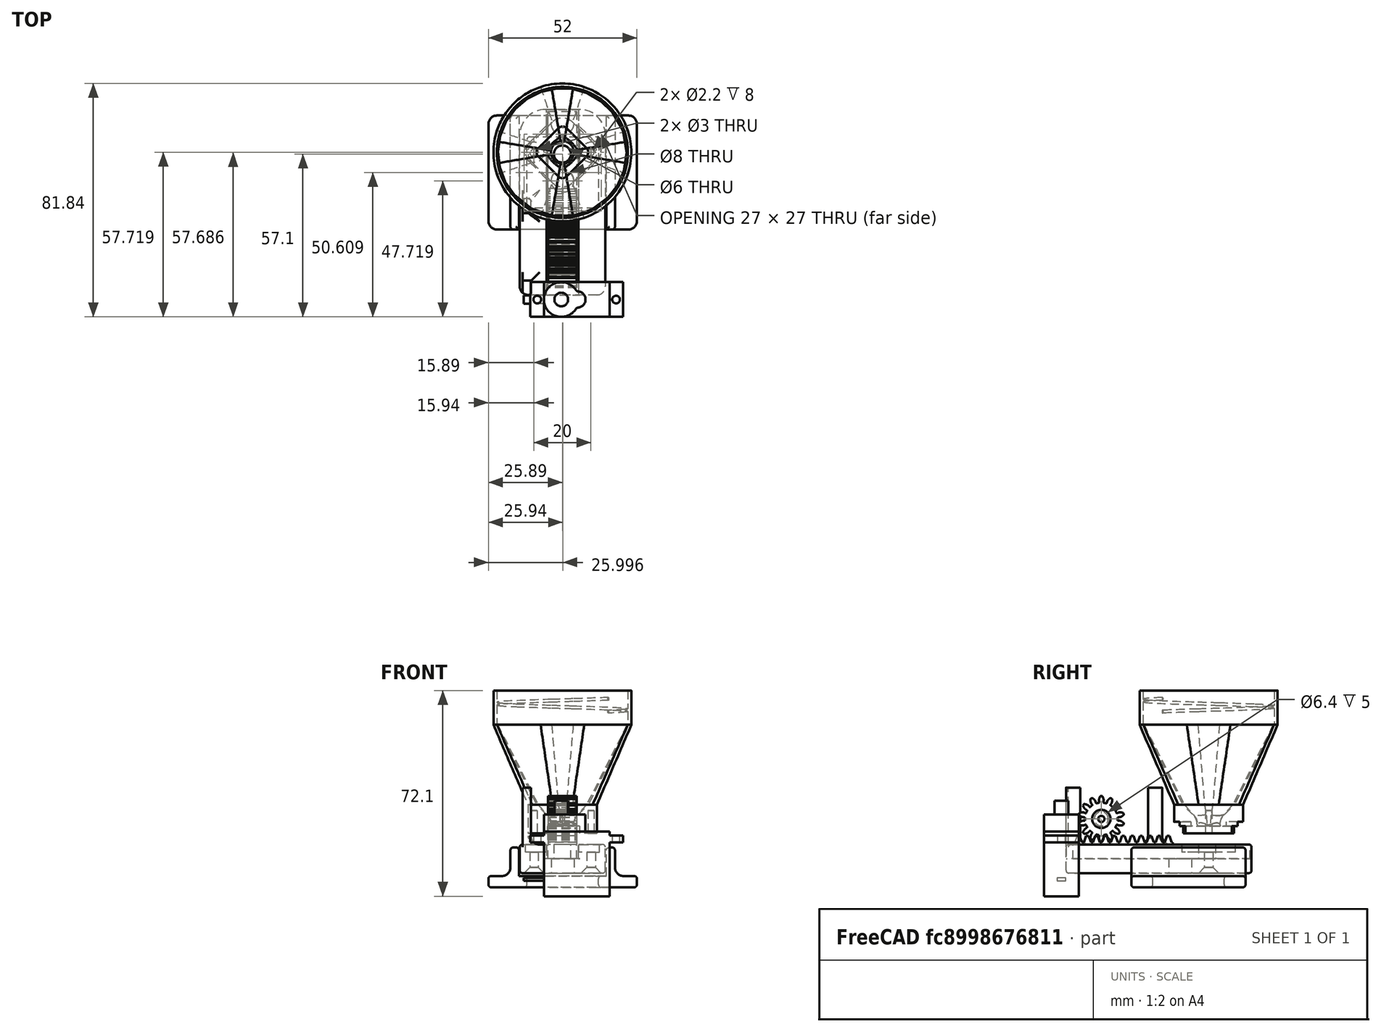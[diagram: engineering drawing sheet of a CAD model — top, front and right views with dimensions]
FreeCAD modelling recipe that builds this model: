
FCSTD DOCUMENT  (FreeCAD 0.19R24267 +148 (Git))
Label: aqua-feeder-v2
License: All rights reserved
LicenseURL: http://en.wikipedia.org/wiki/All_rights_reserved
objects: Sketcher::SketchObject×26, PartDesign::Fillet×15, PartDesign::Pad×11, PartDesign::Pocket×8, PartDesign::Body×6, PartDesign::FeaturePython×2, PartDesign::AdditiveLoft×1, PartDesign::AdditiveHelix×1, Spreadsheet::Sheet×1, App::Part×1, PartDesign::Chamfer×1
note: 108 computed .brp shape members not serialized (recipe doc carries the construction recipe); baked Part::Feature solids carry a one-line shape summary decoded from their .brp

FEATURE [Sketcher::SketchObject] Sketch
  FullyConstrained = true
  MapMode = 5
  Support = -> [XY_Plane]
  expr: Constraints[1] = 45.9 / 2
  expr: Constraints[3] = 45.9 / 2 + 0.6 * 2
  sketch-geometry (2):
    g0: Circle CenterX=0 CenterY=0 CenterZ=0 NormalX=0 NormalY=0 NormalZ=1 AngleXU=0 Radius=22.95
    g1: Circle CenterX=0 CenterY=0 CenterZ=0 NormalX=0 NormalY=0 NormalZ=1 AngleXU=0 Radius=24.15
  constraints (4):
    c: Coincident(g0,g-1)
    c: Radius(g0) = 22.95
    c: Coincident(g1,g0)
    c: Radius(g1) = 24.15
FEATURE [Sketcher::SketchObject] Sketch001
  AttachmentOffset = pos=(0,0,40) rot=(0,0,1;0rad)
  FullyConstrained = true
  MapMode = 5
  Placement = pos=(0,0,40) rot=(0,0,1;0rad)
  Support = -> [XY_Plane]
  sketch-geometry (16):
    g0: LineSegment StartX=-5 StartY=7 StartZ=0 EndX=5 EndY=7 EndZ=0
    g1: LineSegment StartX=7 StartY=5 StartZ=0 EndX=7 EndY=-5 EndZ=0
    g2: LineSegment StartX=5 StartY=-7 StartZ=0 EndX=-5 EndY=-7 EndZ=0
    g3: LineSegment StartX=-7 StartY=-5 StartZ=0 EndX=-7 EndY=5 EndZ=0
    g4: ArcOfCircle CenterX=-5 CenterY=-5 CenterZ=0 NormalX=0 NormalY=0 NormalZ=1 AngleXU=0 Radius=2 StartAngle=3.14159 EndAngle=4.71239
    g5: ArcOfCircle CenterX=5 CenterY=-5 CenterZ=0 NormalX=0 NormalY=0 NormalZ=1 AngleXU=0 Radius=2 StartAngle=4.71239 EndAngle=6.28319
    g6: ArcOfCircle CenterX=5 CenterY=5 CenterZ=0 NormalX=0 NormalY=0 NormalZ=1 AngleXU=0 Radius=2 StartAngle=0 EndAngle=1.5708
    g7: ArcOfCircle CenterX=-5 CenterY=5 CenterZ=0 NormalX=0 NormalY=0 NormalZ=1 AngleXU=0 Radius=2 StartAngle=1.5708 EndAngle=3.14159
    g8: LineSegment StartX=-5 StartY=10 StartZ=0 EndX=5 EndY=10 EndZ=0
    g9: LineSegment StartX=10 StartY=5 StartZ=0 EndX=10 EndY=-5 EndZ=0
    g10: LineSegment StartX=5 StartY=-10 StartZ=0 EndX=-5 EndY=-10 EndZ=0
    g11: LineSegment StartX=-10 StartY=-5 StartZ=0 EndX=-10 EndY=5 EndZ=0
    g12: ArcOfCircle CenterX=5 CenterY=5 CenterZ=0 NormalX=0 NormalY=0 NormalZ=1 AngleXU=0 Radius=5 StartAngle=1.5e-15 EndAngle=1.5708
    g13: ArcOfCircle CenterX=5 CenterY=-5 CenterZ=0 NormalX=0 NormalY=0 NormalZ=1 AngleXU=0 Radius=5 StartAngle=4.71239 EndAngle=6.28319
    g14: ArcOfCircle CenterX=-5 CenterY=-5 CenterZ=0 NormalX=0 NormalY=0 NormalZ=1 AngleXU=0 Radius=5 StartAngle=3.14159 EndAngle=4.71239
    g15: ArcOfCircle CenterX=-5 CenterY=5 CenterZ=0 NormalX=0 NormalY=0 NormalZ=1 AngleXU=0 Radius=5 StartAngle=1.5708 EndAngle=3.14159
  constraints (37):
    c: Horizontal(g0)
    c: Horizontal(g2)
    c: Vertical(g1)
    c: Vertical(g3)
    c: Tangent(g2,g4) = 1.5708
    c: Tangent(g3,g4) = 1.5708
    c: Tangent(g2,g5) = 1.5708
    c: Tangent(g1,g5) = 1.5708
    c: Tangent(g0,g6) = 1.5708
    c: Tangent(g1,g6) = 1.5708
    c: Tangent(g3,g7) = 1.5708
    c: Tangent(g0,g7) = 1.5708
    c: Equal(g6,g5)
    c: Equal(g5,g4)
    c: Equal(g4,g7)
    c: Symmetric(g7,g5,g-1)
    c: Radius(g7) = 2
    c: Horizontal(g8)
    c: Horizontal(g10)
    c: Vertical(g9)
    c: Vertical(g11)
    c: Tangent(g8,g12) = 1.5708
    c: Tangent(g9,g12) = 1.5708
    c: Tangent(g10,g13) = 1.5708
    c: Tangent(g9,g13) = 1.5708
    c: Tangent(g10,g14) = 1.5708
    c: Tangent(g11,g14) = 1.5708
    c: Tangent(g11,g15) = 1.5708
    c: Tangent(g8,g15) = 1.5708
    c: Equal(g15,g12)
    c: Equal(g12,g13)
    c: Equal(g13,g14)
    c: Coincident(g15,g7)
    c: Coincident(g13,g5)
    c: DistanceX(g11,g3) = 3
    c: DistanceX(g11,g9) = 20
    c: DistanceY(g10,g8) = 20
FEATURE [Sketcher::SketchObject] Sketch002  label="thread"
  FullyConstrained = true
  MapMode = 3
  Placement = pos=(0,0,0) rot=(1,0,0;1.5708rad)
  sketch-geometry (2):
    g0: LineSegment StartX=-23 StartY=2.4 StartZ=0 EndX=-23 EndY=3.4 EndZ=0
    g1: ArcOfCircle CenterX=-23 CenterY=2.9 CenterZ=0 NormalX=0 NormalY=0 NormalZ=1 AngleXU=0 Radius=0.5 StartAngle=4.71239 EndAngle=7.85398
  constraints (7):
    c: Vertical(g0)
    c: DistanceY(g-1,g0) = 2.4
    c: Coincident(g1,g0)
    c: Coincident(g1,g0)
    c: PointOnObject(g1,g0)
    c: Radius(g1) = 0.5
    c: DistanceX(g0,g-1) = 23
FEATURE [Sketcher::SketchObject] Sketch004
  AttachmentOffset = pos=(0,0,50) rot=(0,0,1;0rad)
  ExternalGeometry = -> [Sketch001]
  FullyConstrained = false
  MapMode = 5
  Placement = pos=(0,0,50) rot=(0,0,1;0rad)
  Support = -> [XY_Plane]
  sketch-geometry (9):
    g0: Circle CenterX=0 CenterY=0 CenterZ=0 NormalX=0 NormalY=0 NormalZ=1 AngleXU=0 Radius=4
    g1: LineSegment StartX=-5 StartY=10 StartZ=0 EndX=5 EndY=10 EndZ=0
    g2: LineSegment StartX=10 StartY=5 StartZ=0 EndX=10 EndY=-5 EndZ=0
    g3: LineSegment StartX=5 StartY=-10 StartZ=0 EndX=-5 EndY=-10 EndZ=0
    g4: LineSegment StartX=-10 StartY=-5 StartZ=0 EndX=-10 EndY=5 EndZ=0
    g5: ArcOfCircle CenterX=5 CenterY=5 CenterZ=0 NormalX=0 NormalY=0 NormalZ=1 AngleXU=0 Radius=5 StartAngle=-1.8e-15 EndAngle=1.5708
    g6: ArcOfCircle CenterX=5 CenterY=-5 CenterZ=0 NormalX=0 NormalY=0 NormalZ=1 AngleXU=0 Radius=5 StartAngle=4.71239 EndAngle=6.28319
    g7: ArcOfCircle CenterX=-5 CenterY=-5 CenterZ=0 NormalX=0 NormalY=0 NormalZ=1 AngleXU=0 Radius=5 StartAngle=3.14159 EndAngle=4.71239
    g8: ArcOfCircle CenterX=-5 CenterY=5 CenterZ=0 NormalX=0 NormalY=0 NormalZ=1 AngleXU=0 Radius=5 StartAngle=1.5708 EndAngle=3.14159
  constraints (16):
    c: Coincident(g0,g-1)
    c: Radius(g0) = 4
    c: Horizontal(g1)
    c: Horizontal(g3)
    c: Vertical(g4)
    c: Tangent(g1,g5) = 1.5708
    c: Tangent(g2,g5) = 1.5708
    c: Tangent(g3,g6) = 1.5708
    c: Tangent(g2,g6) = 1.5708
    c: Tangent(g3,g7) = 1.5708
    c: Tangent(g4,g7) = 1.5708
    c: Tangent(g4,g8) = 1.5708
    c: Tangent(g1,g8) = 1.5708
    c: Equal(g8,g5)
    c: Equal(g5,g6)
    c: Equal(g6,g7)
FEATURE [Sketcher::SketchObject] Sketch005
  AttachmentOffset = pos=(0,0,12) rot=(0,0,1;0rad)
  FullyConstrained = true
  MapMode = 5
  Placement = pos=(0,0,12) rot=(0,0,1;0rad)
  Support = -> [XY_Plane]
  expr: Constraints[1] = 45.9 / 2
  expr: Constraints[3] = 45.9 / 2 + 0.6 * 2
  sketch-geometry (2):
    g0: Circle CenterX=0 CenterY=0 CenterZ=0 NormalX=0 NormalY=0 NormalZ=1 AngleXU=0 Radius=22.95
    g1: Circle CenterX=0 CenterY=0 CenterZ=0 NormalX=0 NormalY=0 NormalZ=1 AngleXU=0 Radius=24.15
  constraints (4):
    c: Coincident(g0,g-1)
    c: Radius(g0) = 22.95
    c: Coincident(g1,g0)
    c: Radius(g1) = 24.15
FEATURE [Sketcher::SketchObject] Sketch006  label="mount-holes"
  AttachmentOffset = pos=(0,0,50) rot=(0,0,1;0rad)
  FullyConstrained = true
  MapMode = 5
  Placement = pos=(0,0,50) rot=(0,0,1;0rad)
  Support = -> [XY_Plane]
  sketch-geometry (3):
    g0: Circle CenterX=-7.07107 CenterY=7.07107 CenterZ=0 NormalX=0 NormalY=0 NormalZ=1 AngleXU=0 Radius=1.1
    g1: Circle CenterX=7.07107 CenterY=-7.07107 CenterZ=0 NormalX=0 NormalY=0 NormalZ=1 AngleXU=0 Radius=1.1
    g2: LineSegment StartX=7.07107 StartY=-7.07107 StartZ=0 EndX=-7.07107 EndY=7.07107 EndZ=0
  constraints (7):
    c: Symmetric(g1,g0,g-1)
    c: Equal(g0,g1)
    c: Radius(g1) = 1.1
    c: Distance(g1,g0) = 20
    c: Coincident(g2,g1)
    c: Coincident(g2,g0)
    c: Angle(g2,g-1) = 0.785398
FEATURE [Sketcher::SketchObject] Sketch007
  AttachmentOffset = pos=(0,0,45) rot=(0,0,1;0rad)
  ExternalGeometry = -> [Sketch001]
  FullyConstrained = false
  MapMode = 5
  Placement = pos=(0,0,45) rot=(0,0,1;0rad)
  Support = -> [XY_Plane]
  sketch-geometry (9):
    g0: Circle CenterX=0 CenterY=0 CenterZ=0 NormalX=0 NormalY=0 NormalZ=1 AngleXU=0 Radius=4
    g1: LineSegment StartX=-5 StartY=10 StartZ=0 EndX=5 EndY=10 EndZ=0
    g2: LineSegment StartX=10 StartY=5 StartZ=0 EndX=10 EndY=-5 EndZ=0
    g3: LineSegment StartX=5 StartY=-10 StartZ=0 EndX=-5 EndY=-10 EndZ=0
    g4: LineSegment StartX=-10 StartY=-5 StartZ=0 EndX=-10 EndY=5 EndZ=0
    g5: ArcOfCircle CenterX=5 CenterY=5 CenterZ=0 NormalX=0 NormalY=0 NormalZ=1 AngleXU=0 Radius=5 StartAngle=-1.8e-15 EndAngle=1.5708
    g6: ArcOfCircle CenterX=5 CenterY=-5 CenterZ=0 NormalX=0 NormalY=0 NormalZ=1 AngleXU=0 Radius=5 StartAngle=4.71239 EndAngle=6.28319
    g7: ArcOfCircle CenterX=-5 CenterY=-5 CenterZ=0 NormalX=0 NormalY=0 NormalZ=1 AngleXU=0 Radius=5 StartAngle=3.14159 EndAngle=4.71239
    g8: ArcOfCircle CenterX=-5 CenterY=5 CenterZ=0 NormalX=0 NormalY=0 NormalZ=1 AngleXU=0 Radius=5 StartAngle=1.5708 EndAngle=3.14159
  constraints (16):
    c: Coincident(g0,g-1)
    c: Radius(g0) = 4
    c: Horizontal(g1)
    c: Horizontal(g3)
    c: Vertical(g4)
    c: Tangent(g1,g5) = 1.5708
    c: Tangent(g2,g5) = 1.5708
    c: Tangent(g3,g6) = 1.5708
    c: Tangent(g2,g6) = 1.5708
    c: Tangent(g3,g7) = 1.5708
    c: Tangent(g4,g7) = 1.5708
    c: Tangent(g4,g8) = 1.5708
    c: Tangent(g1,g8) = 1.5708
    c: Equal(g8,g5)
    c: Equal(g5,g6)
    c: Equal(g6,g7)
FEATURE [PartDesign::AdditiveLoft] AdditiveLoft  label="body001"
  Closed = false
  Profile = -> Sketch
  Refine = true
  Ruled = true
  Sections = -> [Sketch005,Sketch001,Sketch007,Sketch004]
FEATURE [PartDesign::Pocket] Pocket  label="mount-holes001"
  BaseFeature = -> AdditiveLoft
  Length = 8
  Length2 = 100
  Profile = -> Sketch006
  Type = 0
FEATURE [Sketcher::SketchObject] Sketch008
  AttachmentOffset = pos=(0,0,50) rot=(0,0,1;0rad)
  FullyConstrained = false
  MapMode = 5
  Placement = pos=(0,0,50) rot=(0,0,1;0rad)
  Support = -> [XY_Plane]
  sketch-geometry (5):
    g0: LineSegment StartX=-29.8042 StartY=-29.8042 StartZ=0 EndX=30.9142 EndY=30.9142 EndZ=0
    g1: LineSegment StartX=-25.7953 StartY=-17.3431 StartZ=0 EndX=-17.8757 EndY=-25.2627 EndZ=0
    g2: LineSegment StartX=-17.8757 StartY=-25.2627 StartZ=0 EndX=26.0543 EndY=18.6672 EndZ=0
    g3: LineSegment StartX=26.0543 StartY=18.6672 StartZ=0 EndX=18.1347 EndY=26.5868 EndZ=0
    g4: LineSegment StartX=18.1347 StartY=26.5868 StartZ=0 EndX=-25.7953 EndY=-17.3431 EndZ=0
  constraints (11):
    c: PointOnObject(g-1,g0)
    c: Angle(g-1,g0) = 0.785398
    c: Coincident(g1,g2)
    c: Coincident(g2,g3)
    c: Coincident(g3,g4)
    c: Coincident(g4,g1)
    c: Equal(g1,g3)
    c: Equal(g2,g4)
    c: Perpendicular(g3,g2)
    c: Perpendicular(g0,g3)
    c: Distance(g1) = 11.2
FEATURE [PartDesign::Pocket] Pocket001  label="slider-wedge"
  BaseFeature = -> Pocket
  Length = 2.5
  Length2 = 100
  Profile = -> Sketch008
  Type = 0
FEATURE [PartDesign::AdditiveHelix] AdditiveHelix  label="thread001"
  Angle = 0
  Axis = (-3e-16,3e-16,1)
  Base = (0,0,0)
  BaseFeature = -> Pocket001
  HasBeenEdited = true
  Height = 4.5
  LeftHanded = false
  Mode = 1
  Outside = false
  Pitch = 4.5
  Profile = -> Sketch002
  ReferenceAxis = -> Z_Axis
  Turns = 1
FEATURE [Sketcher::SketchObject] Sketch009
  AttachmentOffset = pos=(0,0,50) rot=(0,0,1;0rad)
  FullyConstrained = false
  MapMode = 5
  Placement = pos=(0,0,50) rot=(0,0,1;0rad)
  Support = -> [XY_Plane]
  sketch-geometry (3):
    g0: Circle CenterX=7.18002 CenterY=7.18002 CenterZ=0 NormalX=0 NormalY=0 NormalZ=1 AngleXU=0 Radius=4
    g1: Circle CenterX=-7.18002 CenterY=-7.18002 CenterZ=0 NormalX=0 NormalY=0 NormalZ=1 AngleXU=0 Radius=4
    g2: LineSegment StartX=-7.18002 StartY=-7.18002 StartZ=0 EndX=7.18002 EndY=7.18002 EndZ=0
  constraints (6):
    c: Symmetric(g1,g0,g-1)
    c: Coincident(g2,g1)
    c: Coincident(g2,g0)
    c: Angle(g2,g-1) = -0.785398
    c: Equal(g1,g0)
    c: Radius(g1) = 4
FEATURE [PartDesign::Pocket] Pocket002  label="air-relief"
  BaseFeature = -> AdditiveHelix
  Length = 4
  Length2 = 100
  Profile = -> Sketch009
  Type = 0
FEATURE [Sketcher::SketchObject] Sketch010
  FullyConstrained = false
  MapMode = 5
  Support = -> [XY_Plane001]
  sketch-geometry (10):
    g0: LineSegment StartX=-45.9619 StartY=-24.7487 StartZ=0 EndX=0 EndY=21.2132 EndZ=0
    g1: LineSegment StartX=0 StartY=21.2132 StartZ=0 EndX=21.2132 EndY=-3.6e-15 EndZ=0
    g2: LineSegment StartX=21.2132 StartY=-3.6e-15 StartZ=0 EndX=-24.7487 EndY=-45.9619 EndZ=0
    g3: LineSegment StartX=-24.7487 StartY=-45.9619 StartZ=0 EndX=-45.9619 EndY=-24.7487 EndZ=0
    g4: LineSegment StartX=-48.6553 StartY=-48.6553 StartZ=0 EndX=36.5487 EndY=36.5487 EndZ=0
    g5: Circle CenterX=0 CenterY=0 CenterZ=0 NormalX=0 NormalY=0 NormalZ=1 AngleXU=0 Radius=4
    g6: Circle CenterX=-7.07107 CenterY=-7.07107 CenterZ=0 NormalX=0 NormalY=0 NormalZ=1 AngleXU=0 Radius=4
    g7: LineSegment StartX=-17.1824 StartY=17.1824 StartZ=0 EndX=25.6869 EndY=-25.6869 EndZ=0
    g8: Circle CenterX=-7.07107 CenterY=7.07107 CenterZ=0 NormalX=0 NormalY=0 NormalZ=1 AngleXU=0 Radius=1.5
    g9: Circle CenterX=7.07107 CenterY=-7.07107 CenterZ=0 NormalX=0 NormalY=0 NormalZ=1 AngleXU=0 Radius=1.5
  constraints (25):
    c: Coincident(g0,g1)
    c: Coincident(g1,g2)
    c: Coincident(g2,g3)
    c: Coincident(g3,g0)
    c: Perpendicular(g3,g2)
    c: Perpendicular(g1,g0)
    c: Equal(g1,g3)
    c: Angle(g-1,g2) = 0.785398
    c: PointOnObject(g-1,g4)
    c: Symmetric(g1,g0,g4)
    c: Distance(g-1,g1) = 15
    c: Coincident(g5,g-1)
    c: Radius(g5) = 4
    c: PointOnObject(g6,g4)
    c: Radius(g6) = 4
    c: Distance(g-1,g6) = 10
    c: PointOnObject(g-1,g7)
    c: Perpendicular(g4,g7)
    c: PointOnObject(g8,g7)
    c: Symmetric(g9,g8,g4)
    c: Equal(g9,g8)
    c: Radius(g9) = 1.5
    c: Distance(g9,g8) = 20
    c: Distance(g2) = 65
    c: Distance(g3) = 30
FEATURE [PartDesign::Pad] Pad
  Direction = (1,1,1)
  Length = 10
  Length2 = 100
  Profile = -> Sketch010
  Type = 0
FEATURE [Sketcher::SketchObject] Sketch011
  AttachmentOffset = pos=(0,0,10) rot=(0,0,1;0rad)
  FullyConstrained = false
  MapMode = 5
  Placement = pos=(0,0,10) rot=(0,0,1;0rad)
  Support = -> [XY_Plane001]
  sketch-geometry (5):
    g0: LineSegment StartX=43.6409 StartY=43.6409 StartZ=0 EndX=-60.5181 EndY=-60.5181 EndZ=0
    g1: LineSegment StartX=-47.3359 StartY=-39.4163 StartZ=0 EndX=26.3866 EndY=34.3061 EndZ=0
    g2: LineSegment StartX=26.3866 StartY=34.3061 StartZ=0 EndX=34.3061 EndY=26.3866 EndZ=0
    g3: LineSegment StartX=34.3061 StartY=26.3866 StartZ=0 EndX=-39.4163 EndY=-47.3359 EndZ=0
    g4: LineSegment StartX=-39.4163 StartY=-47.3359 StartZ=0 EndX=-47.3359 EndY=-39.4163 EndZ=0
  constraints (11):
    c: PointOnObject(g-1,g0)
    c: Angle(g0,g-1) = -0.785398
    c: Coincident(g1,g2)
    c: Coincident(g2,g3)
    c: Coincident(g3,g4)
    c: Coincident(g4,g1)
    c: Perpendicular(g4,g3)
    c: Perpendicular(g2,g1)
    c: Equal(g2,g4)
    c: Symmetric(g2,g1,g0)
    c: Distance(g4) = 11.2
FEATURE [PartDesign::Pocket] Pocket003
  BaseFeature = -> Pad
  Length = 5
  Length2 = 100
  Profile = -> Sketch011
  Type = 0
FEATURE [Spreadsheet::Sheet] Spreadsheet  label="data"
  cells = A2=tolerance; B2(tolerance)=0.3; A3=tolerance1; B3(tolerance1)=0.2; A4=servo_width; B4(servo_width)=32.5; C4=total servo width; A5=servo_mount_width; B5(servo_mount_width)=27.6; C5=distance between mounting hole centers; A6=servo_height; B6(servo_height)=12.2; A7=servo_body_width; B7(servo_body_width)=23; A8=servo_body_depth; B8(servo_body_depth)=18.9; A9=servo_mount_depth; B9(servo_mount_depth)=2.4; C9=thickness of servo mount ears; A10=servo_wire_height; B10(servo_wire_height)=3; A11=servo_wire_depth; B11(servo_wire_depth)=1; A12=servo_wire_pos; B12(servo_wire_pos)=13; A13=servo_base_depth; B13(servo_base_depth)=6; A14=servo_shaft_d; B14(servo_shaft_d)=4.5; A16=bearing_id; B16(bearing_id)=3; A17=bearing_od; B17(bearing_od)=8; A18=bearing_brim; B18(bearing_brim)=9; A20=shaft_to_shaft; B20(shaft_to_shaft)=39; C20=measured
FEATURE [Sketcher::SketchObject] Sketch003  label="shaft"
  FullyConstrained = true
  Placement = pos=(0,0,8.6) rot=(0,0,1;0rad)
  expr: .Placement.Base.z = <<data>>.servo_mount_depth / 2 + 1.4 + <<data>>.servo_base_depth
  expr: Constraints[2] = <<data>>.servo_body_width / 2 - <<data>>.servo_height / 2
  sketch-geometry (1):
    g0: Circle CenterX=-5.4 CenterY=0 CenterZ=0 NormalX=0 NormalY=0 NormalZ=1 AngleXU=0 Radius=2.4
  constraints (3):
    c: Radius(g0) = 2.4
    c: PointOnObject(g0,g-1)
    c: Distance(g-1,g0) = 5.4
FEATURE [Sketcher::SketchObject] Sketch013  label="mount"
  FullyConstrained = true
  MapMode = 5
  Support = -> [XY_Plane005]
  expr: .Constraints.width = <<data>>.servo_width
  expr: .Constraints.height = <<data>>.servo_height
  expr: .Constraints.mount = <<data>>.servo_mount_width
  sketch-geometry (6):
    g0: LineSegment StartX=-16.25 StartY=6.1 StartZ=0 EndX=16.25 EndY=6.1 EndZ=0
    g1: LineSegment StartX=16.25 StartY=6.1 StartZ=0 EndX=16.25 EndY=-6.1 EndZ=0
    g2: LineSegment StartX=16.25 StartY=-6.1 StartZ=0 EndX=-16.25 EndY=-6.1 EndZ=0
    g3: LineSegment StartX=-16.25 StartY=-6.1 StartZ=0 EndX=-16.25 EndY=6.1 EndZ=0
    g4: Circle CenterX=-13.8 CenterY=0 CenterZ=0 NormalX=0 NormalY=0 NormalZ=1 AngleXU=0 Radius=1.35
    g5: Circle CenterX=13.8 CenterY=0 CenterZ=0 NormalX=0 NormalY=0 NormalZ=1 AngleXU=0 Radius=1.35
  constraints (16):
    c: Coincident(g0,g1)
    c: Coincident(g1,g2)
    c: Coincident(g2,g3)
    c: Coincident(g3,g0)
    c: Horizontal(g0)
    c: Horizontal(g2)
    c: Vertical(g1)
    c: Vertical(g3)
    c: Equal(g4,g5)
    c: PointOnObject(g4,g-1)
    c: Symmetric(g4,g5,g-2)
    c: Symmetric(g2,g0,g-1)
    c: DistanceX(g0,g0) = 32.5  'width'
    c: DistanceY(g1,g1) = 12.2  'height'
    c: DistanceX(g4,g5) = 27.6  'mount'
    c: Radius(g4) = 1.35
FEATURE [PartDesign::Pad] Pad003
  Direction = (1,1,1)
  Length = 2.4
  Length2 = 100
  Midplane = true
  Profile = -> Sketch013
  Type = 0
  expr: Length = <<data>>.servo_mount_depth
FEATURE [Sketcher::SketchObject] Sketch014  label="face"
  FullyConstrained = true
  Placement = pos=(0,0,1.2) rot=(0,0,1;0rad)
  expr: .Constraints.body_width = <<data>>.servo_body_width
  expr: .Placement.Base.z = <<data>>.servo_mount_depth / 2
  expr: Constraints[10] = <<data>>.servo_height
  sketch-geometry (4):
    g0: LineSegment StartX=-11.5 StartY=6.1 StartZ=0 EndX=11.5 EndY=6.1 EndZ=0
    g1: LineSegment StartX=11.5 StartY=6.1 StartZ=0 EndX=11.5 EndY=-6.1 EndZ=0
    g2: LineSegment StartX=11.5 StartY=-6.1 StartZ=0 EndX=-11.5 EndY=-6.1 EndZ=0
    g3: LineSegment StartX=-11.5 StartY=-6.1 StartZ=0 EndX=-11.5 EndY=6.1 EndZ=0
  constraints (11):
    c: Coincident(g0,g1)
    c: Coincident(g1,g2)
    c: Coincident(g2,g3)
    c: Coincident(g3,g0)
    c: Horizontal(g0)
    c: Horizontal(g2)
    c: Vertical(g1)
    c: Vertical(g3)
    c: Symmetric(g1,g0,g-1)
    c: DistanceX(g2,g2) = 23  'body_width'
    c: DistanceY(g1,g1) = 12.2
FEATURE [PartDesign::Pad] Pad001
  BaseFeature = -> Pad003
  Direction = (1,1,1)
  Length = 1.4
  Length2 = 100
  Profile = -> Sketch014
  Type = 0
  expr: Length = 1.4
FEATURE [Sketcher::SketchObject] Sketch015  label="shaft_base"
  FullyConstrained = true
  Placement = pos=(0,0,2.6) rot=(0,0,1;0rad)
  expr: Constraints[7] = 5.7 / 2
  expr: .Placement.Base.z = 1.4 + <<data>>.servo_mount_depth / 2
  expr: Constraints[14] = <<data>>.servo_height / 2
  expr: Constraints[15] = <<data>>.servo_body_width / 2 - <<data>>.servo_height / 2
  sketch-geometry (6):
    g0: ArcOfCircle CenterX=-5.4 CenterY=0 CenterZ=0 NormalX=0 NormalY=0 NormalZ=1 AngleXU=0 Radius=6.1 StartAngle=0.570824 EndAngle=5.71236
    g1: ArcOfCircle CenterX=0.25 CenterY=0 CenterZ=0 NormalX=0 NormalY=0 NormalZ=1 AngleXU=0 Radius=2.85 StartAngle=4.79673 EndAngle=7.76964
    g2: GeomPoint X=3.1 Y=0 Z=0
    g3: GeomPoint X=-11.5 Y=0 Z=0
    g4: ArcOfCircle CenterX=0.574336 CenterY=3.83631 CenterZ=0 NormalX=0 NormalY=0 NormalZ=1 AngleXU=0 Radius=1 StartAngle=3.71242 EndAngle=4.62805
    g5: ArcOfCircle CenterX=0.574336 CenterY=-3.83631 CenterZ=0 NormalX=0 NormalY=0 NormalZ=1 AngleXU=0 Radius=1 StartAngle=1.65514 EndAngle=2.57077
  constraints (16):
    c: PointOnObject(g0,g-1)
    c: PointOnObject(g1,g-1)
    c: PointOnObject(g2,g-1)
    c: PointOnObject(g2,g1)
    c: PointOnObject(g3,g0)
    c: PointOnObject(g3,g-1)
    c: DistanceX(g3,g2) = 14.6
    c: Radius(g1) = 2.85
    c: Tangent(g0,g4) = 1.5708
    c: Tangent(g1,g4) = 1.5708
    c: Tangent(g0,g5) = 1.5708
    c: Tangent(g1,g5) = 1.5708
    c: Vertical(g5,g4)
    c: Radius(g5) = 1
    c: Radius(g0) = 6.1
    c: DistanceX(g0,g-1) = 5.4
FEATURE [PartDesign::Pad] Pad002
  BaseFeature = -> Pad001
  Direction = (1,1,1)
  Length = 6
  Length2 = 100
  Profile = -> Sketch015
  Type = 0
  expr: Length = <<data>>.servo_base_depth
FEATURE [PartDesign::Pad] Pad005
  BaseFeature = -> Pad002
  Direction = (1,1,1)
  Length = 4.8
  Length2 = 100
  Profile = -> Sketch003
  Type = 0
FEATURE [Sketcher::SketchObject] Sketch016  label="body"
  ExternalGeometry = -> [Sketch013]
  FullyConstrained = true
  MapMode = 5
  Placement = pos=(0,0,-1.2) rot=(1,0,0;3.14159rad)
  expr: Constraints[10] = <<data>>.servo_body_width
  expr: .Placement.Base.z = -<<data>>.servo_mount_depth / 2
  sketch-geometry (4):
    g0: LineSegment StartX=-11.5 StartY=6.1 StartZ=0 EndX=11.5 EndY=6.1 EndZ=0
    g1: LineSegment StartX=11.5 StartY=6.1 StartZ=0 EndX=11.5 EndY=-6.1 EndZ=0
    g2: LineSegment StartX=11.5 StartY=-6.1 StartZ=0 EndX=-11.5 EndY=-6.1 EndZ=0
    g3: LineSegment StartX=-11.5 StartY=-6.1 StartZ=0 EndX=-11.5 EndY=6.1 EndZ=0
  constraints (11):
    c: Coincident(g0,g1)
    c: Coincident(g1,g2)
    c: Coincident(g2,g3)
    c: Coincident(g3,g0)
    c: Horizontal(g0)
    c: Horizontal(g2)
    c: Vertical(g1)
    c: Vertical(g3)
    c: Symmetric(g0,g1,g-1)
    c: PointOnObject(g0,g-3)
    c: DistanceX(g0,g0) = 23
FEATURE [PartDesign::Pad] Pad004
  BaseFeature = -> Pad005
  Direction = (1,1,1)
  Length = 18.9
  Length2 = 100
  Profile = -> Sketch016
  Type = 0
  expr: Length = <<data>>.servo_body_depth
FEATURE [Sketcher::SketchObject] Sketch012
  FullyConstrained = false
  MapMode = 5
  Placement = pos=(-11.5,0,0) rot=(0.57735,-0.57735,-0.57735;2.0944rad)
  Support = -> [Pad004]
  expr: Constraints[7] = <<data>>.servo_wire_height
  expr: Constraints[8] = <<data>>.servo_wire_depth
  expr: Constraints[11] = <<data>>.servo_wire_pos + <<data>>.servo_mount_depth / 2
  sketch-geometry (5):
    g0: LineSegment StartX=-1.5 StartY=-13.7 StartZ=0 EndX=1.5 EndY=-13.7 EndZ=0
    g1: LineSegment StartX=1.5 StartY=-13.7 StartZ=0 EndX=1.5 EndY=-14.7 EndZ=0
    g2: LineSegment StartX=1.5 StartY=-14.7 StartZ=0 EndX=-1.5 EndY=-14.7 EndZ=0
    g3: LineSegment StartX=-1.5 StartY=-14.7 StartZ=0 EndX=-1.5 EndY=-13.7 EndZ=0
    g4: LineSegment StartX=-3.43751 StartY=-14.2 StartZ=0 EndX=3.43751 EndY=-14.2 EndZ=0
  constraints (12):
    c: Coincident(g0,g1)
    c: Coincident(g1,g2)
    c: Coincident(g2,g3)
    c: Coincident(g3,g0)
    c: Horizontal(g2)
    c: Vertical(g1)
    c: Symmetric(g0,g0,g-2)
    c: DistanceX(g0,g0) = 3
    c: DistanceY(g1,g1) = 1
    c: Symmetric(g4,g4,g-2)
    c: Symmetric(g0,g2,g4)
    c: Distance(g-1,g4) = 14.2
FEATURE [PartDesign::Pad] Pad008
  BaseFeature = -> Pad004
  Direction = (1,1,1)
  Length = 7
  Length2 = 100
  Profile = -> Sketch012
  Type = 0
FEATURE [PartDesign::Body] Body004
  Group = -> [Sketch013,Sketch014,Sketch015,Sketch003,Sketch016,Pad003,Pad001,Pad002,Pad005,Pad004,Sketch012,Pad008]
  Origin = -> Origin004
  Tip = -> Pad008
FEATURE [App::Part] Part  label="MG90"
  Group = -> [Body004]
  Origin = -> Origin005
  Placement = pos=(-20.2721,18.2721,7) rot=(-0.57735,-0.57735,-0.57735;4.18879rad)
FEATURE [PartDesign::FeaturePython] involuterack  # WARN: FeaturePython — macro-defined, semantics opaque (R4)
  AttacherType = Attacher::AttachEngine3D
  Placement = pos=(0,0,0) rot=(0,-1,0;1.5708rad)
  add_endings = true
  beta = 0
  clearance = 0.25
  double_helix = false
  head = 0
  height = 10
  module = 1
  pressure_angle = 20
  properties_from_tool = true
  simplified = false
  teeth = 11
  thickness = 1
  transverse_pitch = 3.14159
  version = 0.0.3
FEATURE [PartDesign::FeaturePython] involutegear  # WARN: FeaturePython — macro-defined, semantics opaque (R4)
  AttacherType = Attacher::AttachEngine3D
  backlash = 0
  beta = 0
  clearance = 0.25
  da = 16
  df = 11.5
  double_helix = false
  dw = 14
  head = 0
  height = 10
  module = 1
  numpoints = 6
  pressure_angle = 20
  properties_from_tool = false
  reversed_backlash = false
  shift = 0
  simple = false
  teeth = 14
  transverse_pitch = 3.14159
  undercut = false
  version = 0.0.3
FEATURE [Sketcher::SketchObject] Sketch017
  AttachmentOffset = pos=(0,0,10) rot=(0,0,1;0rad)
  FullyConstrained = false
  MapMode = 5
  Placement = pos=(0,0,10) rot=(0,0,1;0rad)
  Support = -> [XY_Plane001]
  sketch-geometry (10):
    g0: LineSegment StartX=-20.061 StartY=20.061 StartZ=0 EndX=20.2305 EndY=-20.2305 EndZ=0
    g1: LineSegment StartX=15.0605 StartY=15.0605 StartZ=0 EndX=-15.0604 EndY=-15.0604 EndZ=0
    g2: ArcOfCircle CenterX=-5.6 CenterY=5.6 CenterZ=0 NormalX=0 NormalY=0 NormalZ=1 AngleXU=0 Radius=5 StartAngle=1.5708 EndAngle=3.14159
    g3: ArcOfCircle CenterX=5.6 CenterY=-5.6 CenterZ=0 NormalX=0 NormalY=0 NormalZ=1 AngleXU=0 Radius=5 StartAngle=4.71239 EndAngle=6.28319
    g4: ArcOfCircle CenterX=5.6 CenterY=5.6 CenterZ=0 NormalX=0 NormalY=0 NormalZ=1 AngleXU=0 Radius=5 StartAngle=1.08e-14 EndAngle=1.5708
    g5: ArcOfCircle CenterX=-5.6 CenterY=-5.6 CenterZ=0 NormalX=0 NormalY=0 NormalZ=1 AngleXU=0 Radius=5 StartAngle=3.14159 EndAngle=4.71239
    g6: LineSegment StartX=5.6 StartY=10.6 StartZ=0 EndX=-5.6 EndY=10.6 EndZ=0
    g7: LineSegment StartX=-10.6 StartY=5.6 StartZ=0 EndX=-10.6 EndY=-5.6 EndZ=0
    g8: LineSegment StartX=-5.6 StartY=-10.6 StartZ=0 EndX=5.6 EndY=-10.6 EndZ=0
    g9: LineSegment StartX=10.6 StartY=-5.6 StartZ=0 EndX=10.6 EndY=5.6 EndZ=0
  constraints (22):
    c: PointOnObject(g-1,g0)
    c: PointOnObject(g-1,g1)
    c: Perpendicular(g0,g1)
    c: Angle(g-1,g1) = 0.785398
    c: PointOnObject(g2,g0)
    c: PointOnObject(g4,g1)
    c: Equal(g2,g5)
    c: Equal(g5,g3)
    c: Equal(g3,g4)
    c: Symmetric(g5,g4,g-1)
    c: Symmetric(g3,g2,g-1)
    c: Tangent(g7,g5) = -1.5708
    c: Tangent(g7,g2) = -1.5708
    c: Tangent(g6,g2) = -1.5708
    c: Tangent(g6,g4) = -1.5708
    c: Tangent(g9,g4) = -1.5708
    c: Tangent(g9,g3) = -1.5708
    c: Tangent(g8,g3) = -1.5708
    c: Tangent(g8,g5) = -1.5708
    c: Distance(g5,g3) = 21.2
    c: Perpendicular(g6,g7)
    c: Radius(g2) = 5
FEATURE [PartDesign::Pocket] Pocket004
  BaseFeature = -> Pocket003
  Length = 2.7
  Length2 = 100
  Profile = -> Sketch017
  Refine = true
  Type = 0
FEATURE [Sketcher::SketchObject] Sketch018
  AttachmentOffset = pos=(0,0,-7) rot=(0,0,1;0rad)
  FullyConstrained = false
  MapMode = 5
  Placement = pos=(0,0,-7) rot=(0,0,1;0rad)
  Support = -> [XY_Plane002]
  sketch-geometry (6):
    g0: LineSegment StartX=0 StartY=-1.88496 StartZ=0 EndX=-10 EndY=-1.88496 EndZ=0
    g1: LineSegment StartX=-10 StartY=-1.88496 StartZ=0 EndX=-10 EndY=60 EndZ=0
    g2: LineSegment StartX=-10 StartY=60 StartZ=0 EndX=0 EndY=60 EndZ=0
    g3: LineSegment StartX=0 StartY=60 StartZ=0 EndX=0 EndY=-1.88496 EndZ=0
    g4: LineSegment StartX=-5 StartY=60 StartZ=0 EndX=-5 EndY=-1.88496 EndZ=0
    g5: Circle CenterX=-5 CenterY=45 CenterZ=0 NormalX=0 NormalY=0 NormalZ=1 AngleXU=0 Radius=3
  constraints (17):
    c: Coincident(g0,g1)
    c: Coincident(g1,g2)
    c: Coincident(g2,g3)
    c: Coincident(g3,g0)
    c: Horizontal(g0)
    c: Horizontal(g2)
    c: Vertical(g1)
    c: Vertical(g3)
    c: DistanceX(g2,g2) = 10
    c: PointOnObject(g0,g-2)
    c: Vertical(g4)
    c: Symmetric(g2,g1,g4)
    c: Equal(g4,g3)
    c: DistanceY(g-1,g2) = 60
    c: PointOnObject(g5,g4)
    c: Radius(g5) = 3
    c: Distance(g5,g2) = 15
FEATURE [PartDesign::Pad] Pad009
  BaseFeature = -> involuterack
  Direction = (1,1,1)
  Length = 5
  Length2 = 100
  Placement = pos=(0,0,0) rot=(0,-1,0;1.5708rad)
  Profile = -> Sketch018
  Refine = true
  Type = 0
FEATURE [PartDesign::Body] Body002  label="rail"
  Group = -> [involuterack,Sketch018,Pad009]
  Origin = -> Origin002
  Placement = pos=(0,6,0) rot=(0,0,1;0rad)
  Tip = -> Pad009
FEATURE [Sketcher::SketchObject] Sketch019
  FullyConstrained = true
  MapMode = 5
  Support = -> [XY_Plane003]
  sketch-geometry (1):
    g0: Circle CenterX=0 CenterY=0 CenterZ=0 NormalX=0 NormalY=0 NormalZ=1 AngleXU=0 Radius=2.45
  constraints (2):
    c: Coincident(g0,g-1)
    c: Radius(g0) = 2.45
FEATURE [PartDesign::Pocket] Pocket005
  BaseFeature = -> involutegear
  Length = 4
  Length2 = 100
  Profile = -> Sketch019
  Reversed = true
  Type = 0
FEATURE [Sketcher::SketchObject] Sketch020
  FullyConstrained = true
  MapMode = 5
  Support = -> [XY_Plane003]
  sketch-geometry (1):
    g0: Circle CenterX=0 CenterY=0 CenterZ=0 NormalX=0 NormalY=0 NormalZ=1 AngleXU=0 Radius=1.1
  constraints (2):
    c: Coincident(g0,g-1)
    c: Radius(g0) = 1.1
FEATURE [PartDesign::Pocket] Pocket006
  BaseFeature = -> Pocket005
  Length = 5
  Length2 = 100
  Profile = -> Sketch020
  Reversed = true
  Type = 1
FEATURE [Sketcher::SketchObject] Sketch021
  AttachmentOffset = pos=(0,0,10) rot=(0,0,1;0rad)
  FullyConstrained = true
  MapMode = 5
  Placement = pos=(0,0,10) rot=(0,0,1;0rad)
  Support = -> [XY_Plane003]
  sketch-geometry (1):
    g0: Circle CenterX=0 CenterY=0 CenterZ=0 NormalX=0 NormalY=0 NormalZ=1 AngleXU=0 Radius=3.2
  constraints (2):
    c: Coincident(g0,g-1)
    c: Radius(g0) = 3.2
FEATURE [PartDesign::Pocket] Pocket007
  BaseFeature = -> Pocket006
  Length = 5
  Length2 = 100
  Profile = -> Sketch021
  Type = 0
FEATURE [PartDesign::Body] Body003  label="gear"
  Group = -> [involutegear,Sketch019,Pocket005,Sketch020,Pocket006,Sketch021,Pocket007]
  Origin = -> Origin003
  Placement = pos=(-10,14,7) rot=(0.707107,0,0.707107;3.14159rad)
  Tip = -> Pocket007
FEATURE [PartDesign::Fillet] Fillet
  Base = -> Pocket002 [Edge182]
  BaseFeature = -> Pocket002
  Radius = 5
  SupportTransform = false
FEATURE [Sketcher::SketchObject] Sketch022
  FullyConstrained = true
  MapMode = 5
  Support = -> [XY_Plane]
FEATURE [PartDesign::Body] Body  label="container"
  Group = -> [Sketch,Sketch001,Sketch002,Sketch004,Sketch005,AdditiveLoft,Sketch006,Pocket,Sketch008,Pocket001,AdditiveHelix,Sketch009,Pocket002,Fillet,Sketch022]
  Origin = -> Origin
  Placement = pos=(-5,51.5858,52) rot=(0.382683,0.92388,0;3.14159rad)
  Tip = -> Fillet
FEATURE [Sketcher::SketchObject] Sketch023
  AttachmentOffset = pos=(0,0,10) rot=(0,0,1;0rad)
  ExternalGeometry = -> [Pocket004]
  FullyConstrained = false
  MapMode = 5
  Placement = pos=(0,0,10) rot=(0,0,1;0rad)
  Support = -> [XY_Plane001]
  sketch-geometry (10):
    g0: LineSegment StartX=-49.5453 StartY=-49.5453 StartZ=0 EndX=96.9625 EndY=96.9625 EndZ=0
    g1: LineSegment StartX=-55.2416 StartY=-35.4426 StartZ=0 EndX=3.34841 EndY=23.1474 EndZ=0
    g2: LineSegment StartX=-41.7193 StartY=-21.9203 StartZ=0 EndX=-39.598 EndY=-24.0416 EndZ=0
    g3: LineSegment StartX=-45.2548 StartY=-25.4558 StartZ=0 EndX=-43.1335 EndY=-27.5772 EndZ=0
    g4: LineSegment StartX=-41.7193 StartY=-21.9203 StartZ=0 EndX=-45.2548 EndY=-25.4558 EndZ=0
    g5: LineSegment StartX=-43.1335 StartY=-27.5772 StartZ=0 EndX=-39.598 EndY=-24.0416 EndZ=0
    g6: LineSegment StartX=-24.9609 StartY=-5.16188 StartZ=0 EndX=-22.8395 EndY=-7.2832 EndZ=0
    g7: LineSegment StartX=-22.8395 StartY=-7.2832 StartZ=0 EndX=-19.304 EndY=-3.74767 EndZ=0
    g8: LineSegment StartX=-19.304 StartY=-3.74767 StartZ=0 EndX=-21.4253 EndY=-1.62635 EndZ=0
    g9: LineSegment StartX=-21.4253 StartY=-1.62635 StartZ=0 EndX=-24.9609 EndY=-5.16188 EndZ=0
  constraints (28):
    c: PointOnObject(g-1,g0)
    c: Angle(g0,g-1) = -0.785398
    c: Parallel(g1,g0)
    c: PointOnObject(g2,g1)
    c: Distance(g1,g0) = 14
    c: Perpendicular(g1,g2)
    c: PointOnObject(g3,g1)
    c: PointOnObject(g3,g-3)
    c: PointOnObject(g3,g-3)
    c: Coincident(g4,g2)
    c: Coincident(g4,g3)
    c: Coincident(g5,g3)
    c: Coincident(g5,g2)
    c: Equal(g2,g3)
    c: Distance(g5) = 5
    c: Distance(g2) = 3
    c: PointOnObject(g6,g1)
    c: Coincident(g7,g6)
    c: Coincident(g8,g7)
    c: PointOnObject(g8,g1)
    c: Coincident(g9,g8)
    c: Coincident(g9,g6)
    c: Perpendicular(g1,g6)
    c: Perpendicular(g1,g8)
    c: Equal(g8,g6)
    c: Equal(g6,g2)
    c: Equal(g5,g7)
    c: Distance(g6,g2) = 23.7
FEATURE [PartDesign::Pad] Pad010
  BaseFeature = -> Pocket004
  Direction = (1,1,1)
  Length = 20
  Length2 = 100
  Profile = -> Sketch023
  Refine = true
  Type = 0
FEATURE [PartDesign::Fillet] Fillet001
  Base = -> Pad010 [Edge2,Edge6]
  BaseFeature = -> Pad010
  Radius = 9
  SupportTransform = false
FEATURE [PartDesign::Fillet] Fillet002
  Base = -> Fillet001 [Edge3,Edge15]
  BaseFeature = -> Fillet001
  Radius = 3
  SupportTransform = false
FEATURE [PartDesign::Fillet] Fillet003
  Base = -> Fillet002 [Edge25,Edge33,Edge23,Edge32,Edge34]
  BaseFeature = -> Fillet002
  Radius = 3
  SupportTransform = false
FEATURE [PartDesign::Fillet] Fillet004
  Base = -> Fillet003 [Edge12,Edge88]
  BaseFeature = -> Fillet003
  Radius = 0.9
  SupportTransform = false
FEATURE [PartDesign::Chamfer] Chamfer
  Angle = 45
  Base = -> Fillet004 [Edge92,Edge93]
  BaseFeature = -> Fillet004
  ChamferType = 0
  FlipDirection = false
  Size = 2
  Size2 = 1
  SupportTransform = false
FEATURE [PartDesign::Fillet] Fillet005
  Base = -> Chamfer [Edge31]
  BaseFeature = -> Chamfer
  Radius = 0.9
  SupportTransform = false
FEATURE [PartDesign::Fillet] Fillet006
  Base = -> Fillet005 [Edge140,Edge136]
  BaseFeature = -> Fillet005
  Radius = 1
  SupportTransform = false
FEATURE [PartDesign::Fillet] Fillet007
  Base = -> Fillet006 [Edge51,Edge90]
  BaseFeature = -> Fillet006
  Radius = 0.5
  SupportTransform = false
FEATURE [PartDesign::Fillet] Fillet008
  Base = -> Fillet007 [Edge46,Edge101]
  BaseFeature = -> Fillet007
  Radius = 0.3
  SupportTransform = false
FEATURE [PartDesign::Fillet] Fillet009
  Base = -> Fillet008 [Edge88]
  BaseFeature = -> Fillet008
  Radius = 1
  SupportTransform = false
FEATURE [PartDesign::Body] Body001  label="base"
  Group = -> [Sketch010,Pad,Sketch011,Pocket003,Sketch017,Pocket004,Sketch023,Pad010,Fillet001,Fillet002,Fillet003,Fillet004,Chamfer,Fillet005,Fillet006,Fillet007,Fillet008,Fillet009]
  Origin = -> Origin001
  Placement = pos=(-4.94975,51.6188,-12) rot=(0,0,1;0.785398rad)
  Tip = -> Fillet009
FEATURE [Sketcher::SketchObject] Sketch024
  FullyConstrained = false
  MapMode = 5
  Support = -> [XY_Plane006]
  sketch-geometry (10):
    g0: LineSegment StartX=-30.8937 StartY=61.5091 StartZ=0 EndX=21.1063 EndY=61.5091 EndZ=0
    g1: LineSegment StartX=21.1063 StartY=61.5091 StartZ=0 EndX=21.1063 EndY=21.5091 EndZ=0
    g2: LineSegment StartX=21.1063 StartY=21.5091 StartZ=0 EndX=-30.8937 EndY=21.5091 EndZ=0
    g3: LineSegment StartX=-30.8937 StartY=21.5091 StartZ=0 EndX=-30.8937 EndY=61.5091 EndZ=0
    g4: LineSegment StartX=-17.3937 StartY=54.0091 StartZ=0 EndX=7.60625 EndY=54.0091 EndZ=0
    g5: LineSegment StartX=7.60625 StartY=54.0091 StartZ=0 EndX=7.60625 EndY=29.0091 EndZ=0
    g6: LineSegment StartX=7.60625 StartY=29.0091 StartZ=0 EndX=-17.3937 EndY=29.0091 EndZ=0
    g7: LineSegment StartX=-17.3937 StartY=29.0091 StartZ=0 EndX=-17.3937 EndY=54.0091 EndZ=0
    g8: LineSegment StartX=-30.8937 StartY=41.5091 StartZ=0 EndX=21.1063 EndY=41.5091 EndZ=0
    g9: LineSegment StartX=-4.89375 StartY=21.5091 StartZ=0 EndX=-4.89375 EndY=61.5091 EndZ=0
  constraints (27):
    c: Coincident(g0,g1)
    c: Coincident(g1,g2)
    c: Coincident(g2,g3)
    c: Coincident(g3,g0)
    c: Horizontal(g0)
    c: Horizontal(g2)
    c: Vertical(g1)
    c: Vertical(g3)
    c: Coincident(g4,g5)
    c: Coincident(g5,g6)
    c: Coincident(g6,g7)
    c: Coincident(g7,g4)
    c: Horizontal(g4)
    c: Horizontal(g6)
    c: Vertical(g7)
    c: PointOnObject(g8,g3)
    c: PointOnObject(g8,g1)
    c: PointOnObject(g9,g2)
    c: PointOnObject(g9,g0)
    c: Symmetric(g8,g8,g9)
    c: Symmetric(g5,g4,g8)
    c: Symmetric(g4,g4,g9)
    c: Symmetric(g9,g9,g8)
    c: Equal(g5,g4)
    c: DistanceY(g1,g1) = 40
    c: DistanceY(g5,g5) = 25
    c: DistanceX(g0,g0) = 52
FEATURE [PartDesign::Pad] Pad011
  Direction = (1,1,1)
  Length = 4
  Length2 = 100
  Profile = -> Sketch024
  Type = 0
FEATURE [Sketcher::SketchObject] Sketch025
  AttachmentOffset = pos=(0,0,4) rot=(0,0,1;0rad)
  ExternalGeometry = -> [Pad011]
  FullyConstrained = true
  MapMode = 5
  Placement = pos=(0,0,4) rot=(0,0,1;0rad)
  Support = -> [XY_Plane006]
  sketch-geometry (9):
    g0: LineSegment StartX=-4.89375 StartY=61.5091 StartZ=0 EndX=-4.89375 EndY=21.5091 EndZ=0
    g1: LineSegment StartX=-23.1937 StartY=61.5091 StartZ=0 EndX=-20.1937 EndY=61.5091 EndZ=0
    g2: LineSegment StartX=-20.1937 StartY=61.5091 StartZ=0 EndX=-20.1937 EndY=21.5091 EndZ=0
    g3: LineSegment StartX=-20.1937 StartY=21.5091 StartZ=0 EndX=-23.1937 EndY=21.5091 EndZ=0
    g4: LineSegment StartX=-23.1937 StartY=21.5091 StartZ=0 EndX=-23.1937 EndY=61.5091 EndZ=0
    g5: LineSegment StartX=10.4063 StartY=61.5091 StartZ=0 EndX=13.4063 EndY=61.5091 EndZ=0
    g6: LineSegment StartX=13.4063 StartY=61.5091 StartZ=0 EndX=13.4063 EndY=21.5091 EndZ=0
    g7: LineSegment StartX=13.4063 StartY=21.5091 StartZ=0 EndX=10.4063 EndY=21.5091 EndZ=0
    g8: LineSegment StartX=10.4063 StartY=21.5091 StartZ=0 EndX=10.4063 EndY=61.5091 EndZ=0
  constraints (26):
    c: PointOnObject(g0,g-3)
    c: PointOnObject(g0,g-4)
    c: Symmetric(g-3,g-3,g0)
    c: Coincident(g1,g2)
    c: Coincident(g2,g3)
    c: Coincident(g3,g4)
    c: Coincident(g4,g1)
    c: Horizontal(g1)
    c: Horizontal(g3)
    c: Vertical(g2)
    c: Vertical(g4)
    c: PointOnObject(g1,g-3)
    c: PointOnObject(g2,g-4)
    c: Coincident(g5,g6)
    c: Coincident(g6,g7)
    c: Coincident(g7,g8)
    c: Coincident(g8,g5)
    c: Horizontal(g5)
    c: Horizontal(g7)
    c: Vertical(g6)
    c: Vertical(g8)
    c: PointOnObject(g6,g-4)
    c: Equal(g5,g1)
    c: DistanceX(g1,g1) = 3
    c: Symmetric(g1,g5,g0)
    c: DistanceX(g1,g5) = 30.6
FEATURE [PartDesign::Pad] Pad012
  BaseFeature = -> Pad011
  Direction = (1,1,1)
  Length = 10
  Length2 = 100
  Profile = -> Sketch025
  Refine = true
  Type = 0
FEATURE [PartDesign::Fillet] Fillet010
  Base = -> Pad012 [Edge2,Edge1,Edge13,Edge12]
  BaseFeature = -> Pad012
  Radius = 3
  SupportTransform = false
FEATURE [PartDesign::Fillet] Fillet011
  Base = -> Fillet010 [Edge55,Edge21]
  BaseFeature = -> Fillet010
  Radius = 3
  SupportTransform = false
FEATURE [PartDesign::Fillet] Fillet012
  Base = -> Fillet011 [Edge28]
  BaseFeature = -> Fillet011
  Radius = 1
  SupportTransform = false
FEATURE [PartDesign::Fillet] Fillet013
  Base = -> Fillet012 [Edge24,Edge35,Edge37,Edge40,Edge38,Edge9,Edge12,Edge44,Edge45,Edge39]
  BaseFeature = -> Fillet012
  Radius = 1
  SupportTransform = false
FEATURE [PartDesign::Fillet] Fillet014
  Base = -> Fillet013 [Face35,Face34,Face36,Face37]
  BaseFeature = -> Fillet013
  Radius = 1
  SupportTransform = false
FEATURE [PartDesign::Body] Body005  label="adapter"
  Group = -> [Sketch024,Pad011,Sketch025,Pad012,Fillet010,Fillet011,Fillet012,Fillet013,Fillet014]
  Origin = -> Origin006
  Placement = pos=(0,3,-17) rot=(0,0,1;0rad)
  Tip = -> Fillet014
